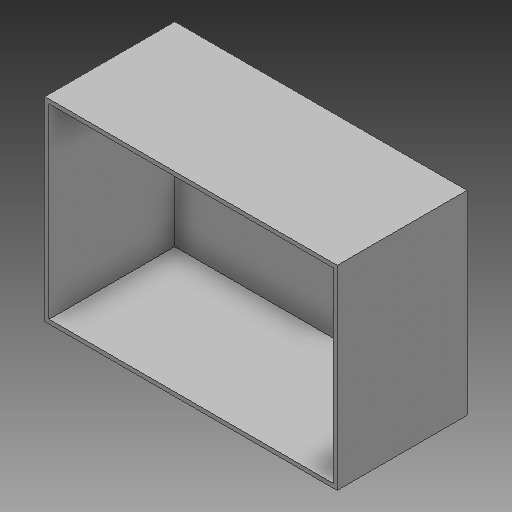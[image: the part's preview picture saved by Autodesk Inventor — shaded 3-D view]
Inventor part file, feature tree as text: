
AUTODESK INVENTOR PART (.ipt)
format: ipt  version: 2019 (Build 230136000, 136)  size: 134,656 bytes
history: native  units: in
note: dims shown in document units (in); Inventor stores cm internally (conversion verified against a paired STEP export)
features: extrude x2, sketch x1, plane x1
ambient origin geometry x8: Origin, YZ Plane, XZ Plane, XY Plane, X Axis, Y Axis, Z Axis, Center Point
bodies: Solid1 (feature_tree)
feature tree (4):
  sketch  "Sketch1"  dims[d0=24.0in d1=36.0in d2=0.5in d3=0.5in d4=0.5in d5=0.5in d6=16.0in d7=0.0in d8=0.5in d9=0.0in]
  extrude  "Extrusion1"  Depth=36.0in
  extrude  "Extrusion2"  Depth=0.5in
  plane  "Work Plane1"
